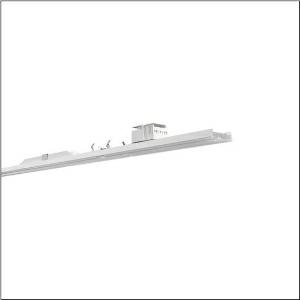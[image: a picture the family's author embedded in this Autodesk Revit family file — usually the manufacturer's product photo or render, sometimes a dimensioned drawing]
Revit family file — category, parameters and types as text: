
# Revit family: licross_r__11_recessed_ho_51tl12dn4dxl3c_dd05
name_source: partatom
category: Lighting Fixtures
units: mm (PartAtom-declared; Revit-internal decimal feet)

## family parameters
Cut with Voids When Loaded = No
Host = Face
Light Source = No
Part Type = Normal
Room Calculation Point = No
Round Connector Dimension = Use Diameter
Shared = No

## types (1)
- --- (1 x LED, 880 lm, 5 W, 4000K)
    Apparent Load = 5 VA
    CIE Flux Codes = 66 91 98 100 100
    Color Rendering = 80
    Color Temperature = 4000K
    Default Elevation = 1800 mm
    Description = Licross® 11 Recessed HO, luminaire insert, of sheet steel, galvanised, coil coated, white, length: 1.500mm, width: 66mm, height: 67mm, LED rated luminous flux: 13.000lm, light colour: 840, control gear: DALI 2, control gear: ECG DALI, with plug, 6-pole, with phase selection, for trunking rail, 14-core, mains connection: 220..240V, AC/DC, 0/50..60Hz, for emergency light function, halogen-free wiring, charging phase on R (wire number 6), converter,control gear: single battery element, battery: LiFeP04, 9Ah, primary optical cover: cover, of PMMA, light emission: direct distribution, protection rating (complete): IP40, insulation class (complete): insulation class I (protective earthing), certification: CE, UKCA, protection symbol: D if used in an environment without relevant dust loads with corresponding accessories, permissible ambient temperature for indoor applications: +5..+30°C, standard: EN 60598-2-22, corresponds to IFS (International Featured Standards) requirements for safety and quality in the food industry, reducing of maximum allowable ambient temperature of 5°C with ceiling mounting, LABS conformity tested according to VDMA 24364:2018-05, packaging unit: 1 piece
    Height = 58 mm
    Lamp = 1 x LED
    Lamp Light Flux = 880 lm
    Lamp Power = 5 W
    Lamp count = 1
    Length = 1500 mm
    Luminous efficacy = 176 lm/W
    Manufacturer = Siteco
    ModVariant = No
    Model = 51TL12DN4DXL3C
    Mounting Place = Ceiling
    Mounting Type = Pendant
    Number of Poles = 1
    OnlyDefault = Yes
    Power Factor = 1
    Product Name = Licross® 11 Recessed HO
    Product group = luminaire insert
    ProductGroupID = 902
    Protection Class = Protection class I
    Protection Degree = IP 40
    RLX_Detail_Level = 1
    RlxData = <blob elided: 22977 chars, md5=bca55acc>
    Socket = socket
    Standby Power = 0 W
    System Light Flux = 880 lm
    System Power = 5 W
    Type Comments = : emergency light operation: 3 h
    Type Image = l_1266722.jpg
    URL = http://relux.com
    VarID = @adj_125817
    Voltage = 0 V
    Weight = 0.00 kg
    Width = 66 mm

## geometry (parser evidence)
native form markers: Blend x4, Sweep x10
no freeform markers — native parametric forms only
